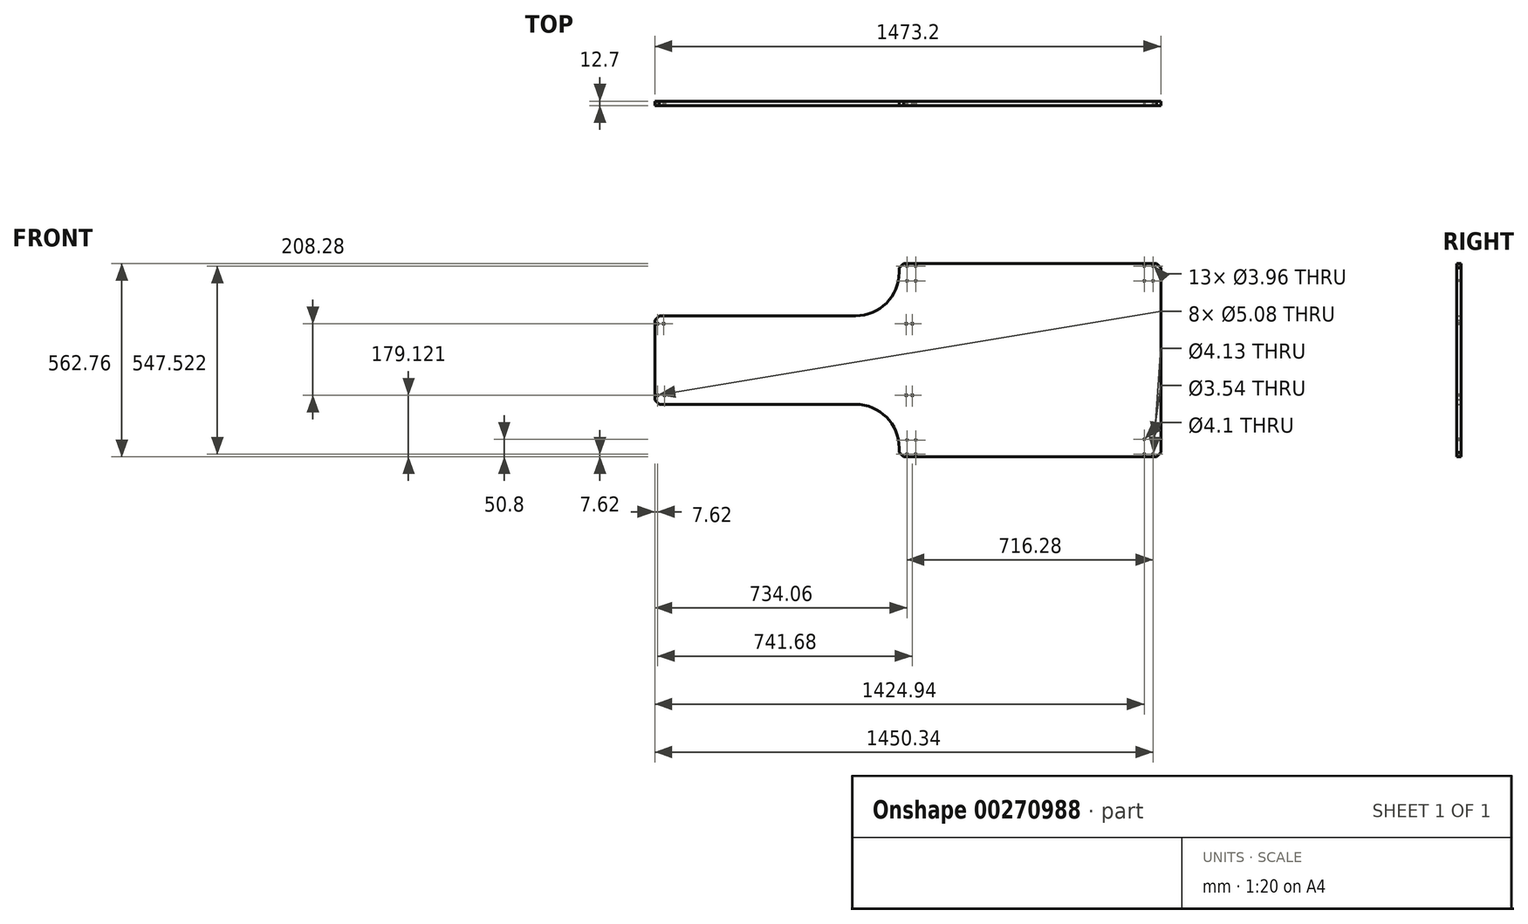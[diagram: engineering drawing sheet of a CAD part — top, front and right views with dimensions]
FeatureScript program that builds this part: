
annotation { "Feature Type Name" : "Feature", "Feature Type Description" : "" }
export const myFeature = defineFeature(function(context is Context, id is Id, definition is map)
    precondition{}
    {
        {
            var Q0;
            Q0=qCreatedBy(makeId("Front.planeOp"),FACE);
            var sketch = newSketch(context, id + "F0", { "sketchPlane" : qUnion([Q0])});
            skLineSegment(sketch, "E0.bottom", {"start": v(0, 0) * mm, "end": v(762, 0) * mm});
            skLineSegment(sketch, "E0.top", {"start": v(0, 562.76) * mm, "end": v(762, 562.76) * mm});
            skLineSegment(sketch, "E0.left", {"start": v(0, 0) * mm, "end": v(0, 25.4) * mm});
            skLineSegment(sketch, "E0.right", {"start": v(762, 0) * mm, "end": v(762, 562.76) * mm});
            skLineSegment(sketch, "E1.bottom", {"start": v(-127, 410.36) * mm, "end": v(-711.2, 410.36) * mm});
            skLineSegment(sketch, "E1.top", {"start": v(-127, 152.4) * mm, "end": v(-711.2, 152.4) * mm});
            skLineSegment(sketch, "E1.right", {"start": v(-711.2, 410.36) * mm, "end": v(-711.2, 152.4) * mm});
            skLineSegment(sketch, "E2.trimOffspring", {"start": v(0, 537.36) * mm, "end": v(0, 562.76) * mm});
            skPoint(sketch, "E3.visualSharp", {"position": v(0, 410.36) * mm});
            skArc(sketch, "E3.filletArc", {"start": v(-127, 410.36) * mm, "mid": v(-37.2, 447.56) * mm, "end": v(0, 537.36) * mm});
            skPoint(sketch, "E4.visualSharp", {"position": v(0, 152.4) * mm});
            skArc(sketch, "E4.filletArc", {"start": v(0, 25.4) * mm, "mid": v(-37.2, 115.2) * mm, "end": v(-127, 152.4) * mm});
            skSolve(sketch);
        }
        {
            var Q0;
            Q0=makeQuery(id+"F0.imprint","IMPRINT",FACE,{"disambiguationData":[TD([[makeQuery(id+"F0.imprint","IMPRINT",EDGE,{"derivedFrom":sQuery(id+"F0.wireOp",EDGE,"E0.bottom")}),1.0]])]});
            extrude(context, id + "F1", {"entities" : qUnion([Q0]), "depth" : 12.7 * mm});
        }
        {
            var Q0;
            Q0=makeQuery(id+"F1.opExtrude","SWEPT_EDGE",EDGE,{"disambiguationData":[OSD([sQuery(id+"F0.wireOp",EDGE,"E1.bottom"),sQuery(id+"F0.wireOp",EDGE,"E1.right")])]});
            var Q1;
            Q1=makeQuery(id+"F1.opExtrude","SWEPT_EDGE",EDGE,{"disambiguationData":[OSD([sQuery(id+"F0.wireOp",EDGE,"E1.top"),sQuery(id+"F0.wireOp",EDGE,"E1.right")])]});
            var Q2;
            Q2=makeQuery(id+"F1.opExtrude","SWEPT_EDGE",EDGE,{"disambiguationData":[OSD([sQuery(id+"F0.wireOp",EDGE,"E0.bottom"),sQuery(id+"F0.wireOp",EDGE,"E0.left")])]});
            var Q3;
            Q3=makeQuery(id+"F1.opExtrude","SWEPT_EDGE",EDGE,{"disambiguationData":[OSD([sQuery(id+"F0.wireOp",EDGE,"E0.top"),sQuery(id+"F0.wireOp",EDGE,"E2.trimOffspring")])]});
            var Q4;
            Q4=makeQuery(id+"F1.opExtrude","SWEPT_EDGE",EDGE,{"disambiguationData":[OSD([sQuery(id+"F0.wireOp",EDGE,"E0.top"),sQuery(id+"F0.wireOp",EDGE,"E0.right")])]});
            var Q5;
            Q5=makeQuery(id+"F1.opExtrude","SWEPT_EDGE",EDGE,{"disambiguationData":[OSD([sQuery(id+"F0.wireOp",EDGE,"E0.bottom"),sQuery(id+"F0.wireOp",EDGE,"E0.right")])]});
            chamfer(context, id + "F2", {"entities" : qUnion([Q0, Q1, Q2, Q3, Q4, Q5]), "width" : 12.7 * mm, "tangentPropagation" : true});
        }
        {
            var Q0;
            Q0=makeQuery(id+"F1.opExtrude","CAP_FACE",FACE,{"disambiguationData":[OSD([sQuery(id+"F0.wireOp",EDGE,"E0.bottom"),sQuery(id+"F0.wireOp",EDGE,"E0.top"),sQuery(id+"F0.wireOp",EDGE,"E0.left"),sQuery(id+"F0.wireOp",EDGE,"E0.right"),sQuery(id+"F0.wireOp",EDGE,"E1.bottom"),sQuery(id+"F0.wireOp",EDGE,"E1.top"),sQuery(id+"F0.wireOp",EDGE,"E1.right"),sQuery(id+"F0.wireOp",EDGE,"E2.trimOffspring"),sQuery(id+"F0.wireOp",EDGE,"E3.filletArc"),sQuery(id+"F0.wireOp",EDGE,"E4.filletArc")])],"isStart":false});
            var sketch = newSketch(context, id + "F3", { "sketchPlane" : qUnion([Q0])});
            skPoint(sketch, "E5", {"position": v(332.7, 355.6) * mm});
            skPoint(sketch, "E6", {"position": v(332.7, 205.59) * mm});
            skPoint(sketch, "E7", {"position": v(586.7, 205.59) * mm});
            skPoint(sketch, "E8", {"position": v(586.7, 355.6) * mm});
            skPoint(sketch, "E9", {"position": v(691.59, 205.59) * mm});
            skPoint(sketch, "E10", {"position": v(742.39, 205.59) * mm});
            skPoint(sketch, "E11", {"position": v(738.42, 383.39) * mm});
            skPoint(sketch, "E12", {"position": v(687.62, 383.39) * mm});
            skSolve(sketch);
        }
        {
            var Q0;
            {var subQ3=sQuery(id+"F0.wireOp",EDGE,"E3.filletArc");Q0=makeQuery(id+"F3.imprint","IMPRINT",FACE,{"disambiguationData":[TD([[makeQuery(id+"F3.imprint","IMPRINT",EDGE,{"derivedFrom":makeQuery(id+"F1.opExtrude","CAP_EDGE",EDGE,{"disambiguationData":[OSD([subQ3])],"isStart":false})}),-1.0]])]});}
            var sketch = newSketch(context, id + "F4", { "sketchPlane" : qUnion([Q0])});
            skCircle(sketch, "E13", {"center": v(713.74, 7.62) * mm, "radius": 1.98 * mm});
            skCircle(sketch, "E14", {"center": v(739.14, 7.62) * mm, "radius": 2.07 * mm});
            skCircle(sketch, "E15", {"center": v(739.14, 50.8) * mm, "radius": 1.77 * mm});
            skCircle(sketch, "E16", {"center": v(713.74, 50.8) * mm, "radius": 2.05 * mm});
            skCircle(sketch, "E17", {"center": v(713.74, 555.14) * mm, "radius": 1.98 * mm});
            skCircle(sketch, "E18", {"center": v(739.14, 555.14) * mm, "radius": 1.98 * mm});
            skCircle(sketch, "E19", {"center": v(739.14, 511.96) * mm, "radius": 1.98 * mm});
            skCircle(sketch, "E20", {"center": v(713.74, 511.96) * mm, "radius": 1.98 * mm});
            skCircle(sketch, "E21", {"center": v(22.86, 555.14) * mm, "radius": 1.98 * mm});
            skCircle(sketch, "E22", {"center": v(48.26, 555.14) * mm, "radius": 1.98 * mm});
            skCircle(sketch, "E23", {"center": v(48.26, 511.96) * mm, "radius": 1.98 * mm});
            skCircle(sketch, "E24", {"center": v(22.86, 511.96) * mm, "radius": 1.98 * mm});
            skCircle(sketch, "E25", {"center": v(22.86, 7.62) * mm, "radius": 1.98 * mm});
            skCircle(sketch, "E26", {"center": v(48.26, 7.62) * mm, "radius": 1.98 * mm});
            skCircle(sketch, "E27", {"center": v(48.26, 48.82) * mm, "radius": 1.98 * mm});
            skCircle(sketch, "E28", {"center": v(22.86, 48.82) * mm, "radius": 1.98 * mm});
            skSolve(sketch);
        }
        {
            var Q0;
            Q0 = qSketchRegion(id + "F4", true);
            extrude(context, id + "F5", {"entities" : qUnion([Q0]), "operationType" : NewBodyOperationType.REMOVE, "endBound" : BoundingType.THROUGH_ALL, "oppositeDirection" : true, "depth" : 25.4 * mm});
        }
        {
            var Q0;
            {var subQ3=sQuery(id+"F0.wireOp",EDGE,"E3.filletArc");Q0=makeQuery(id+"F3.imprint","IMPRINT",FACE,{"disambiguationData":[TD([[makeQuery(id+"F3.imprint","IMPRINT",EDGE,{"derivedFrom":makeQuery(id+"F1.opExtrude","CAP_EDGE",EDGE,{"disambiguationData":[OSD([subQ3])],"isStart":false})}),-1.0]])]});}
            var sketch = newSketch(context, id + "F6", { "sketchPlane" : qUnion([Q0])});
            skCircle(sketch, "E29", {"center": v(-703.58, 387.4) * mm, "radius": 2.54 * mm});
            skCircle(sketch, "E30", {"center": v(-685.8, 387.4) * mm, "radius": 2.54 * mm});
            skCircle(sketch, "E31", {"center": v(20.32, 387.4) * mm, "radius": 2.54 * mm});
            skCircle(sketch, "E32", {"center": v(38.1, 387.4) * mm, "radius": 2.54 * mm});
            skCircle(sketch, "E33", {"center": v(-703.58, 179.12) * mm, "radius": 2.54 * mm});
            skCircle(sketch, "E34", {"center": v(-683.26, 179.12) * mm, "radius": 2.54 * mm});
            skCircle(sketch, "E35", {"center": v(20.32, 179.12) * mm, "radius": 2.54 * mm});
            skCircle(sketch, "E36", {"center": v(38.1, 179.12) * mm, "radius": 2.54 * mm});
            skSolve(sketch);
        }
        {
            var Q0;
            Q0 = qSketchRegion(id + "F6", true);
            extrude(context, id + "F7", {"entities" : qUnion([Q0]), "operationType" : NewBodyOperationType.REMOVE, "endBound" : BoundingType.THROUGH_ALL, "oppositeDirection" : true, "depth" : 25.4 * mm});
        }
    });
